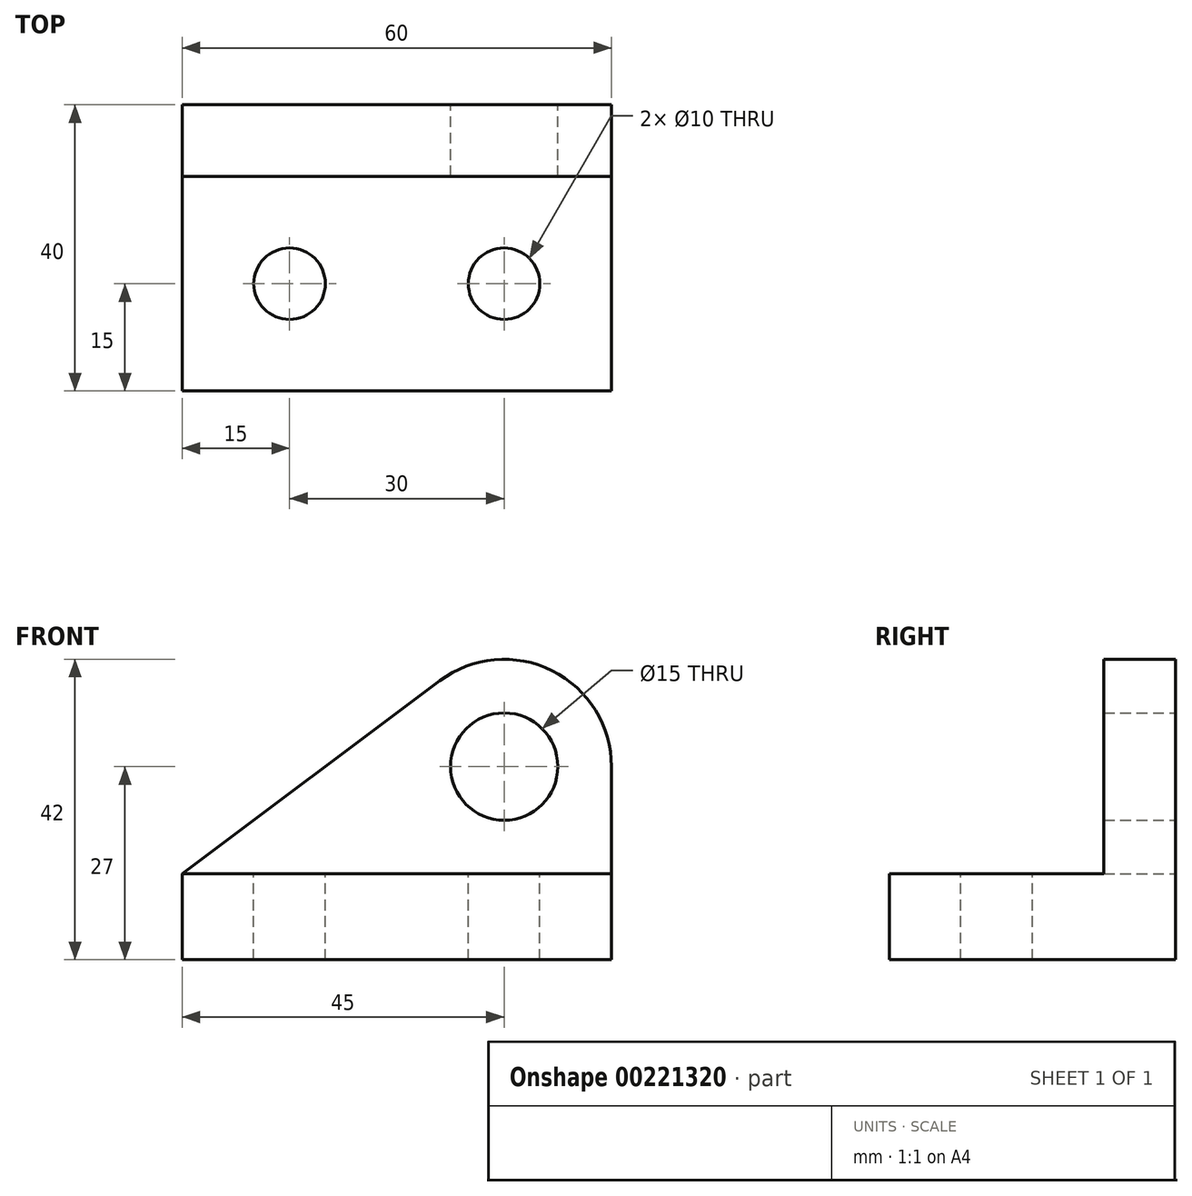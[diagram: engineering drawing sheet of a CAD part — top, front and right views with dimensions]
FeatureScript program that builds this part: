
annotation { "Feature Type Name" : "Feature", "Feature Type Description" : "" }
export const myFeature = defineFeature(function(context is Context, id is Id, definition is map)
    precondition{}
    {
        {
            var Q0;
            Q0=qCreatedBy(makeId("Front.planeOp"),FACE);
            var sketch = newSketch(context, id + "F0", { "sketchPlane" : qUnion([Q0])});
            skLineSegment(sketch, "E0", {"start": v(0, 0) * mm, "end": v(60, 0) * mm});
            skLineSegment(sketch, "E1", {"start": v(60, 0) * mm, "end": v(60, 12) * mm});
            skLineSegment(sketch, "E2", {"start": v(60, 12) * mm, "end": v(0, 12) * mm});
            skLineSegment(sketch, "E3", {"start": v(0, 12) * mm, "end": v(0, 0) * mm});
            skCircle(sketch, "E4", {"center": v(45, 27) * mm, "radius": 7.5 * mm});
            skArc(sketch, "E5", {"start": v(60, 27) * mm, "mid": v(51.7, 40.42) * mm, "end": v(36, 39) * mm});
            skLineSegment(sketch, "E6", {"start": v(60, 27) * mm, "end": v(60, 12) * mm});
            skLineSegment(sketch, "E7", {"start": v(0, 12) * mm, "end": v(36, 39) * mm});
            skSolve(sketch);
        }
        {
            var Q0;
            Q0=makeQuery(id+"F0.imprint","IMPRINT",FACE,{"disambiguationData":[TD([[makeQuery(id+"F0.imprint","IMPRINT",EDGE,{"derivedFrom":sQuery(id+"F0.wireOp",EDGE,"E0")}),1.0]])]});
            extrude(context, id + "F1", {"entities" : qUnion([Q0]), "depth" : 40 * mm});
        }
        {
            var Q0;
            Q0=makeQuery(id+"F0.imprint","IMPRINT",FACE,{"disambiguationData":[TD([[makeQuery(id+"F0.imprint","IMPRINT",EDGE,{"derivedFrom":sQuery(id+"F0.wireOp",EDGE,"E2")}),-1.0]])]});
            extrude(context, id + "F2", {"entities" : qUnion([Q0]), "operationType" : NewBodyOperationType.ADD, "depth" : 10 * mm});
        }
        {
            var Q0;
            Q0=makeQuery(id+"F1.opExtrude","SWEPT_FACE",FACE,{"disambiguationData":[OSD([sQuery(id+"F0.wireOp",EDGE,"E2")])]});
            var sketch = newSketch(context, id + "F3", { "sketchPlane" : qUnion([Q0])});
            skCircle(sketch, "E8", {"center": v(15, -25) * mm, "radius": 5 * mm});
            skCircle(sketch, "E9", {"center": v(45, -25) * mm, "radius": 5 * mm});
            skSolve(sketch);
        }
        {
            var Q0;
            Q0=makeQuery(id+"F3.imprint","IMPRINT",FACE,{"disambiguationData":[TD([[makeQuery(id+"F3.imprint","IMPRINT",EDGE,{"derivedFrom":sQuery(id+"F3.wireOp",EDGE,"E8")}),1.0]])]});
            var Q1;
            Q1=makeQuery(id+"F3.imprint","IMPRINT",FACE,{"disambiguationData":[TD([[makeQuery(id+"F3.imprint","IMPRINT",EDGE,{"derivedFrom":sQuery(id+"F3.wireOp",EDGE,"E9")}),1.0]])]});
            extrude(context, id + "F4", {"entities" : qUnion([Q0, Q1]), "operationType" : NewBodyOperationType.REMOVE, "endBound" : BoundingType.THROUGH_ALL, "oppositeDirection" : true, "depth" : 25 * mm});
        }
    });
